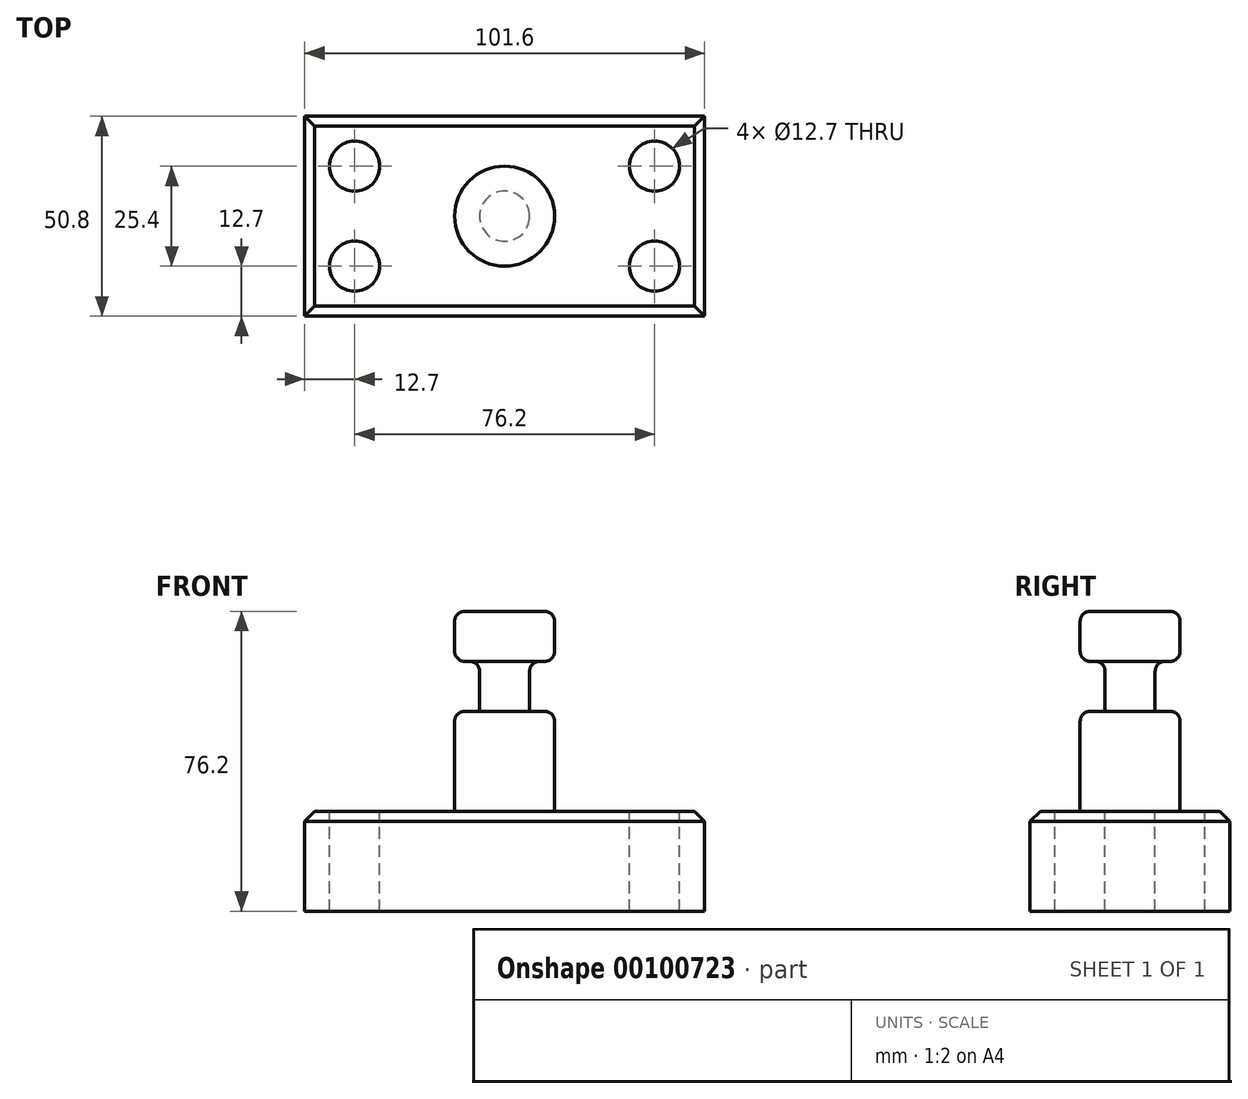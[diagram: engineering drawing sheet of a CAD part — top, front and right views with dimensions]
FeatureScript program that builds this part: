
annotation { "Feature Type Name" : "Feature", "Feature Type Description" : "" }
export const myFeature = defineFeature(function(context is Context, id is Id, definition is map)
    precondition{}
    {
        {
            var Q0;
            Q0=qCreatedBy(makeId("Top.planeOp"),FACE);
            var sketch = newSketch(context, id + "F0", { "sketchPlane" : qUnion([Q0])});
            skLineSegment(sketch, "E0.bottom", {"start": v(50.8, 25.4) * mm, "end": v(-50.8, 25.4) * mm});
            skLineSegment(sketch, "E0.top", {"start": v(50.8, -25.4) * mm, "end": v(-50.8, -25.4) * mm});
            skLineSegment(sketch, "E0.left", {"start": v(50.8, 25.4) * mm, "end": v(50.8, -25.4) * mm});
            skLineSegment(sketch, "E0.right", {"start": v(-50.8, 25.4) * mm, "end": v(-50.8, -25.4) * mm});
            skPoint(sketch, "E0.middle", {"position": v(0, 0) * mm});
            skSolve(sketch);
        }
        {
            var Q0;
            Q0=makeQuery(id+"F0.imprint","IMPRINT",FACE,{"disambiguationData":[TD([[makeQuery(id+"F0.imprint","IMPRINT",EDGE,{"derivedFrom":sQuery(id+"F0.wireOp",EDGE,"E0.bottom")}),1.0]])]});
            extrude(context, id + "F1", {"entities" : qUnion([Q0]), "depth" : 25.4 * mm});
        }
        {
            var Q0;
            Q0=makeQuery(id+"F1.opExtrude","CAP_FACE",FACE,{"disambiguationData":[OSD([sQuery(id+"F0.wireOp",EDGE,"E0.bottom"),sQuery(id+"F0.wireOp",EDGE,"E0.top"),sQuery(id+"F0.wireOp",EDGE,"E0.left"),sQuery(id+"F0.wireOp",EDGE,"E0.right")])],"isStart":false});
            var sketch = newSketch(context, id + "F2", { "sketchPlane" : qUnion([Q0])});
            skCircle(sketch, "E1", {"center": v(-38.1, 12.7) * mm, "radius": 6.35 * mm});
            skCircle(sketch, "E2", {"center": v(38.1, 12.7) * mm, "radius": 6.35 * mm});
            skCircle(sketch, "E3", {"center": v(-38.1, -12.7) * mm, "radius": 6.35 * mm});
            skCircle(sketch, "E4", {"center": v(38.1, -12.7) * mm, "radius": 6.35 * mm});
            skSolve(sketch);
        }
        {
            var Q0;
            Q0=makeQuery(id+"F2.imprint","IMPRINT",FACE,{"disambiguationData":[TD([[makeQuery(id+"F2.imprint","IMPRINT",EDGE,{"derivedFrom":sQuery(id+"F2.wireOp",EDGE,"E1")}),1.0]])]});
            var Q1;
            Q1=makeQuery(id+"F2.imprint","IMPRINT",FACE,{"disambiguationData":[TD([[makeQuery(id+"F2.imprint","IMPRINT",EDGE,{"derivedFrom":sQuery(id+"F2.wireOp",EDGE,"E3")}),1.0]])]});
            var Q2;
            Q2=makeQuery(id+"F2.imprint","IMPRINT",FACE,{"disambiguationData":[TD([[makeQuery(id+"F2.imprint","IMPRINT",EDGE,{"derivedFrom":sQuery(id+"F2.wireOp",EDGE,"E4")}),1.0]])]});
            var Q3;
            Q3=makeQuery(id+"F2.imprint","IMPRINT",FACE,{"disambiguationData":[TD([[makeQuery(id+"F2.imprint","IMPRINT",EDGE,{"derivedFrom":sQuery(id+"F2.wireOp",EDGE,"E2")}),1.0]])]});
            extrude(context, id + "F3", {"entities" : qUnion([Q0, Q1, Q2, Q3]), "operationType" : NewBodyOperationType.REMOVE, "endBound" : BoundingType.THROUGH_ALL, "oppositeDirection" : true, "depth" : 25.4 * mm});
        }
        {
            var Q0;
            Q0=qCreatedBy(makeId("Front.planeOp"),FACE);
            var sketch = newSketch(context, id + "F4", { "sketchPlane" : qUnion([Q0])});
            skLineSegment(sketch, "E5.bottom", {"start": v(0, 25.4) * mm, "end": v(-12.7, 25.4) * mm});
            skLineSegment(sketch, "E5.top", {"start": v(0, 76.2) * mm, "end": v(-12.7, 76.2) * mm});
            skLineSegment(sketch, "E5.left", {"start": v(0, 25.4) * mm, "end": v(0, 76.2) * mm});
            skLineSegment(sketch, "E5.right", {"start": v(-12.7, 25.4) * mm, "end": v(-12.7, 76.2) * mm});
            skSolve(sketch);
        }
        {
            var Q0;
            Q0=makeQuery(id+"F4.imprint","IMPRINT",FACE,{"disambiguationData":[TD([[makeQuery(id+"F4.imprint","IMPRINT",EDGE,{"derivedFrom":sQuery(id+"F4.wireOp",EDGE,"E5.bottom")}),-1.0]])]});
            var Q1;
            Q1=sQuery(id+"F4.wireOp",EDGE,"E5.left");
            revolve(context, id + "F5", {"operationType" : NewBodyOperationType.ADD, "entities" : qUnion([Q0]), "axis" : qUnion([Q1]), "revolveType" : RevolveType.FULL});
        }
        {
            var Q0;
            Q0=qCreatedBy(makeId("Front.planeOp"),FACE);
            var sketch = newSketch(context, id + "F6", { "sketchPlane" : qUnion([Q0])});
            skLineSegment(sketch, "E6.bottom", {"start": v(6.35, 50.8) * mm, "end": v(17.98, 50.8) * mm});
            skLineSegment(sketch, "E6.top", {"start": v(6.35, 63.5) * mm, "end": v(17.98, 63.5) * mm});
            skLineSegment(sketch, "E6.left", {"start": v(6.35, 50.8) * mm, "end": v(6.35, 63.5) * mm});
            skLineSegment(sketch, "E6.right", {"start": v(17.98, 50.8) * mm, "end": v(17.98, 63.5) * mm});
            skLineSegment(sketch, "E7", {"start": v(0, 0) * mm, "end": v(0, 87) * mm, "construction": true});
            skSolve(sketch);
        }
        {
            var Q0;
            Q0=makeQuery(id+"F6.imprint","IMPRINT",FACE,{"disambiguationData":[TD([[makeQuery(id+"F6.imprint","IMPRINT",EDGE,{"derivedFrom":sQuery(id+"F6.wireOp",EDGE,"E6.bottom")}),1.0]])]});
            var Q1;
            Q1=sQuery(id+"F6.wireOp",EDGE,"E7");
            revolve(context, id + "F7", {"operationType" : NewBodyOperationType.REMOVE, "entities" : qUnion([Q0]), "axis" : qUnion([Q1]), "revolveType" : RevolveType.FULL, "oppositeDirection" : true});
        }
        {
            var Q0;
            Q0=makeQuery(id+"F7.boolean.opBoolean","INTERSECT",EDGE,{"derivedFrom":[makeQuery(id+"F5.opRevolve","SWEPT_FACE",FACE,{"disambiguationData":[OSD([sQuery(id+"F4.wireOp",EDGE,"E5.right")])]}),makeQuery(id+"F7.opRevolve","SWEPT_FACE",FACE,{"disambiguationData":[OSD([sQuery(id+"F6.wireOp",EDGE,"E6.bottom")])]})]});
            var Q1;
            Q1=makeQuery(id+"F7.boolean.opBoolean","COPY",EDGE,{"derivedFrom":makeQuery(id+"F7.opRevolve","SWEPT_EDGE",EDGE,{"disambiguationData":[OSD([sQuery(id+"F6.wireOp",EDGE,"E6.top"),sQuery(id+"F6.wireOp",EDGE,"E6.left")])]})});
            var Q2;
            Q2=makeQuery(id+"F7.boolean.opBoolean","INTERSECT",EDGE,{"derivedFrom":[makeQuery(id+"F5.opRevolve","SWEPT_FACE",FACE,{"disambiguationData":[OSD([sQuery(id+"F4.wireOp",EDGE,"E5.right")])]}),makeQuery(id+"F7.opRevolve","SWEPT_FACE",FACE,{"disambiguationData":[OSD([sQuery(id+"F6.wireOp",EDGE,"E6.top")])]})]});
            var Q3;
            Q3=makeQuery(id+"F5.opRevolve","SWEPT_EDGE",EDGE,{"disambiguationData":[OSD([sQuery(id+"F4.wireOp",EDGE,"E5.bottom"),sQuery(id+"F4.wireOp",EDGE,"E5.right")])]});
            var Q4;
            Q4=makeQuery(id+"F5.opRevolve","SWEPT_EDGE",EDGE,{"disambiguationData":[OSD([sQuery(id+"F4.wireOp",EDGE,"E5.top"),sQuery(id+"F4.wireOp",EDGE,"E5.right")])]});
            fillet(context, id + "F8", {"entities" : qUnion([Q0, Q1, Q2, Q3, Q4]), "radius" : 2.54 * mm, "tangentPropagation" : true, "allowEdgeOverflow" : false});
        }
        {
            var Q0;
            Q0=makeQuery(id+"F1.opExtrude","CAP_EDGE",EDGE,{"disambiguationData":[OSD([sQuery(id+"F0.wireOp",EDGE,"E0.top")])],"isStart":false});
            var Q1;
            Q1=makeQuery(id+"F1.opExtrude","CAP_EDGE",EDGE,{"disambiguationData":[OSD([sQuery(id+"F0.wireOp",EDGE,"E0.right")])],"isStart":false});
            var Q2;
            Q2=makeQuery(id+"F1.opExtrude","CAP_EDGE",EDGE,{"disambiguationData":[OSD([sQuery(id+"F0.wireOp",EDGE,"E0.bottom")])],"isStart":false});
            var Q3;
            Q3=makeQuery(id+"F1.opExtrude","CAP_EDGE",EDGE,{"disambiguationData":[OSD([sQuery(id+"F0.wireOp",EDGE,"E0.left")])],"isStart":false});
            chamfer(context, id + "F9", {"entities" : qUnion([Q0, Q1, Q2, Q3]), "width" : 2.54 * mm});
        }
    });
